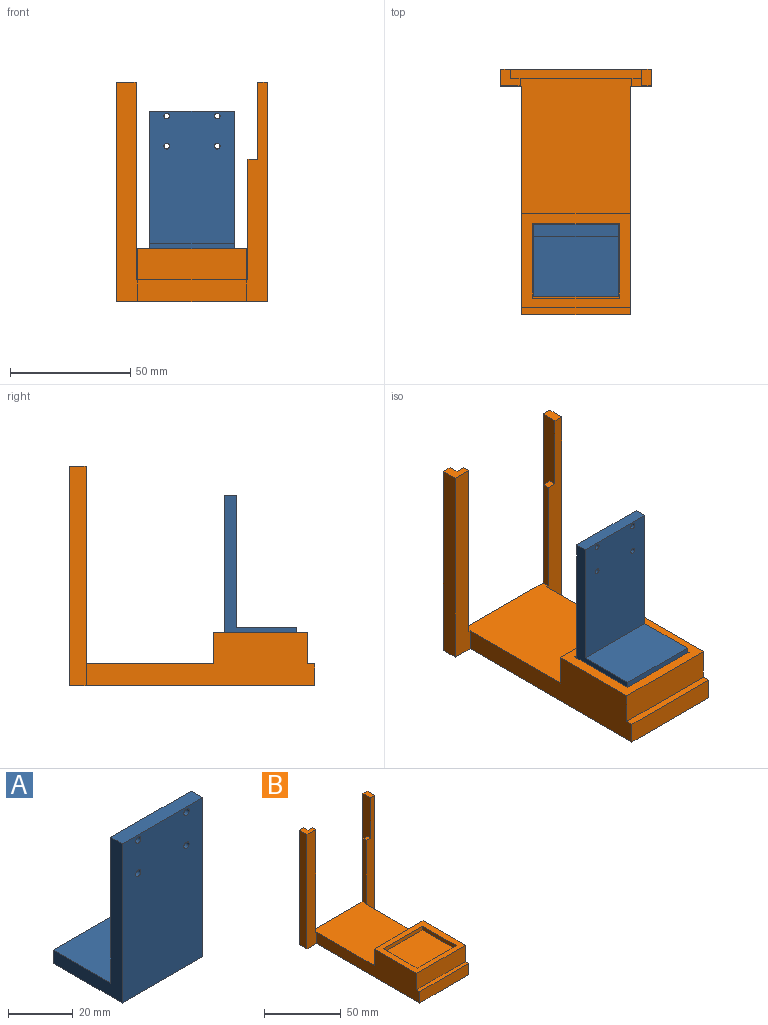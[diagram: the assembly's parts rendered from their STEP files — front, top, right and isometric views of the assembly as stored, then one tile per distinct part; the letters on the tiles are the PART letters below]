
ASSEMBLY  parts=2 mates=1
PART A: 12 faces, bbox 35x30x60 mm
  f0: plane 35x5mm, normal (0,1,0), area 175mm2, adj f1,f2,f3,f4
  f1: plane 60x30mm, normal (-1,0,0), area 425mm2, adj f0,f3,f4,f5,f6,f7
  f2: plane 60x30mm, normal (1,0,0), area 425mm2, adj f0,f3,f4,f5,f6,f7
  f3: plane 35x25mm, normal (0,0,1), area 875mm2, adj f0,f1,f2,f5
  f4: plane 35x30mm, normal (0,0,-1), area 1050mm2, adj f0,f1,f2,f6
  f5: plane 55x35mm, normal (0,1,0), area 1908.4mm2, adj f1,f2,f3,f7,f8,f9,f10,f11
  f6: plane 60x35mm, normal (0,-1,0), area 2083.4mm2, adj f1,f2,f4,f7,f8,f9,f10,f11
  f7: plane 35x5mm, normal (0,0,1), area 175mm2, adj f1,f2,f5,f6
  f8: cylinder r=1.15mm len=5mm, axis (0,-1,0), area 36.1mm2, adj f5,f6
  f9: cylinder r=1.15mm len=5mm, axis (0,-1,0), area 36.1mm2, adj f5,f6
  f10: cylinder r=1.15mm len=5mm, axis (0,-1,0), area 36.1mm2, adj f5,f6
  f11: cylinder r=1.15mm len=5mm, axis (0,-1,0), area 36.1mm2, adj f5,f6
PART B: 28 faces, bbox 62.5x102x91 mm
  f0: plane 45x39mm, normal (0,0,1), area 639mm2, adj f18,f19,f21,f22,f23,f24,f25,f26
  f1: plane 45x3mm, normal (0,0,1), area 135mm2, adj f18,f19,f20,f22
  f2: plane 91x8.75mm, normal (0,-1,0), area 606.8mm2, adj f3,f5,f7,f8,f13,f14,f15,f19
  f3: plane 87x7mm, normal (-1,0,0), area 444mm2, adj f2,f5,f9,f12,f13,f17
  f4: plane 8x7mm, normal (0,0,1), area 40mm2, adj f6,f9,f10,f11,f16,f17
  f5: plane 7x4mm, normal (0,0,1), area 28mm2, adj f2,f3,f8,f9
  f6: plane 91x7mm, normal (-1,0,0), area 637mm2, adj f4,f7,f9,f10
  f7: plane 102x62.5mm, normal (0,0,-1), area 4712.5mm2, adj f2,f6,f8,f9,f10,f18,f19,f20
  f8: plane 91x7mm, normal (1,0,0), area 637mm2, adj f2,f5,f7,f9
  f9: plane 91x62.5mm, normal (0,1,0), area 946mm2, adj f3,f4,f5,f6,f7,f8,f11,f12
  f10: plane 91x8.75mm, normal (0,-1,0), area 734.7mm2, adj f4,f6,f7,f15,f16,f18
  f11: plane 87x4mm, normal (1,0,0), area 348mm2, adj f4,f9,f12,f17
  f12: plane 54.5x4mm, normal (0,0,1), area 218mm2, adj f3,f9,f11,f17
  f13: plane 4x3mm, normal (0,0,1), area 12mm2, adj f2,f3,f14,f17
  f14: plane 50x3mm, normal (-1,0,0), area 150mm2, adj f2,f13,f15,f17
  f15: plane 56x46.5mm, normal (0,0,1), area 2524.5mm2, adj f2,f10,f14,f16,f17,f18,f19,f21
  f16: plane 82x3mm, normal (1,0,0), area 246mm2, adj f4,f10,f15,f17
  f17: plane 87x54.5mm, normal (0,1,0), area 800.5mm2, adj f3,f4,f11,f12,f13,f14,f15,f16
  f18: plane 95x22mm, normal (-1,0,0), area 1362mm2, adj f0,f1,f7,f10,f15,f20,f21,f22
  f19: plane 95x22mm, normal (1,0,0), area 1362mm2, adj f0,f1,f2,f7,f15,f20,f21,f22
  f20: plane 45x9mm, normal (0,-1,0), area 405mm2, adj f1,f7,f18,f19
  f21: plane 45x13mm, normal (0,1,0), area 585mm2, adj f0,f15,f18,f19
  f22: plane 45x13mm, normal (0,-1,0), area 585mm2, adj f0,f1,f18,f19
  f23: plane 36x3mm, normal (0,-1,0), area 108mm2, adj f0,f24,f26,f27
  f24: plane 31x3mm, normal (1,0,0), area 93mm2, adj f0,f23,f25,f27
  f25: plane 36x3mm, normal (0,1,0), area 108mm2, adj f0,f24,f26,f27
  f26: plane 31x3mm, normal (-1,0,0), area 93mm2, adj f0,f23,f25,f27
  f27: plane 36x31mm, normal (0,0,1), area 1116mm2, adj f23,f24,f25,f26
PLACE A rot(axis=(0,0,1),180deg) t=(-24.65,16.73,1.51)mm
PLACE B t=(-7.15,74.23,30.01)mm
MATE fastened A.f4 <-> B.f27  axis (0,0,-1) through (-7.15,1.73,1.51)mm
